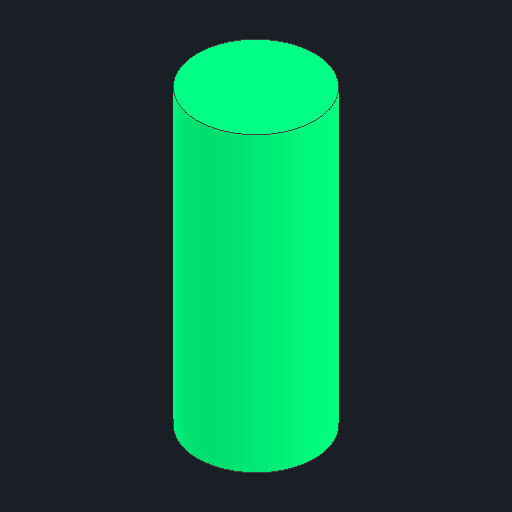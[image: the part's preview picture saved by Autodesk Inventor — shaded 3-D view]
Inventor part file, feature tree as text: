
AUTODESK INVENTOR PART (.ipt)
format: ipt  version: 2025.2 (Build 292293000, 293)  size: 83,456 bytes
history: native  units: in
note: dims shown in document units (in); Inventor stores cm internally (conversion verified against a paired STEP export)
features: other x3, sketch x1
ambient origin geometry x8: Origin, YZ Plane, XZ Plane, XY Plane, X Axis, Y Axis, Z Axis, Center Point
bodies: Solid1 (feature_tree)
feature tree (4):
  other  "26650(Green)_MIR.ipt"
  other  "Solid1::26650(Green)_MIR.ipt"
  other  "TaggingFeature1"
  sketch  "Sketch1"  dims[d0=0.3937in]
